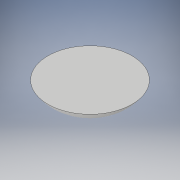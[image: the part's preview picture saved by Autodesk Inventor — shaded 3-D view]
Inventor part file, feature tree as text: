
AUTODESK INVENTOR PART (.ipt)
format: ipt  version: 2019.4 (Build 234330000, 330)  size: 115,712 bytes
history: native  units: mm
features: other x1, revolve x1, sketch x1
ambient origin geometry x8: Origin, YZ Plane, XZ Plane, XY Plane, X Axis, Y Axis, Z Axis, Center Point
bodies: Body1 (feature_tree)
feature tree (3):
  other  "Sólido1"
  revolve  "Revolución1"  [1 undecoded]
  sketch  "Boceto1"  dims[d1=1500.0mm d2=4000.0mm d3=90.0deg]
note: 1 required parameter value undecoded (feature->parameter linkage not recoverable at this tier; creation-order binding heuristic only, values carry confidence <= 0.55)
